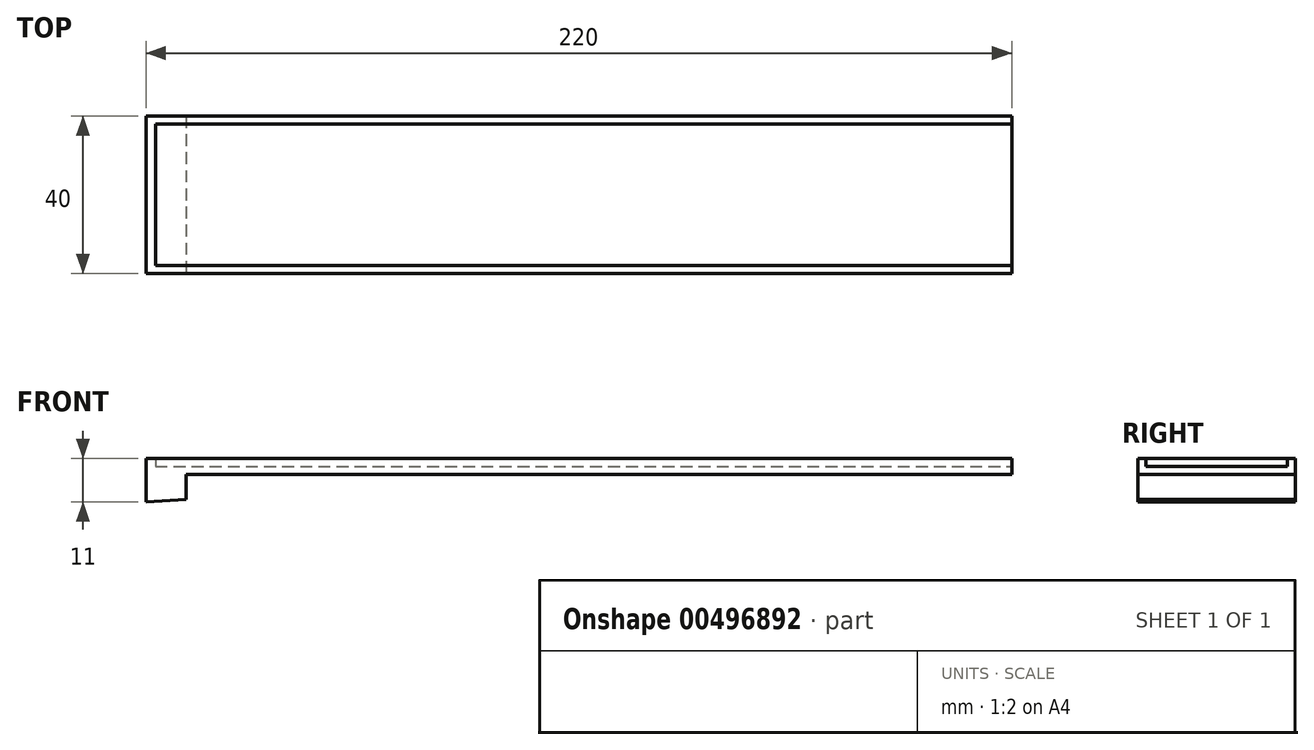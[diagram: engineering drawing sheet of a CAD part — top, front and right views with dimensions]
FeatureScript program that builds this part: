
annotation { "Feature Type Name" : "Feature", "Feature Type Description" : "" }
export const myFeature = defineFeature(function(context is Context, id is Id, definition is map)
    precondition{}
    {
        {
            var Q0;
            Q0=qCreatedBy(makeId("Top.planeOp"),FACE);
            var sketch = newSketch(context, id + "F0", { "sketchPlane" : qUnion([Q0])});
            skLineSegment(sketch, "E0.bottom", {"start": v(-60.42, 25.47) * mm, "end": v(159.58, 25.47) * mm});
            skLineSegment(sketch, "E0.top", {"start": v(-60.42, -14.53) * mm, "end": v(159.58, -14.53) * mm});
            skLineSegment(sketch, "E0.left", {"start": v(-60.42, 25.47) * mm, "end": v(-60.42, -14.53) * mm});
            skLineSegment(sketch, "E0.right", {"start": v(159.58, 25.47) * mm, "end": v(159.58, -14.53) * mm});
            skSolve(sketch);
        }
        {
            var Q0;
            Q0=makeQuery(id+"F0.imprint","IMPRINT",FACE,{"disambiguationData":[TD([[makeQuery(id+"F0.imprint","IMPRINT",EDGE,{"derivedFrom":sQuery(id+"F0.wireOp",EDGE,"E0.bottom")}),-1.0]])]});
            extrude(context, id + "F1", {"entities" : qUnion([Q0]), "depth" : 2 * mm});
        }
        {
            var Q0;
            Q0=makeQuery(id+"F1.opExtrude","CAP_FACE",FACE,{"disambiguationData":[OSD([sQuery(id+"F0.wireOp",EDGE,"E0.bottom"),sQuery(id+"F0.wireOp",EDGE,"E0.top"),sQuery(id+"F0.wireOp",EDGE,"E0.left"),sQuery(id+"F0.wireOp",EDGE,"E0.right")])],"isStart":true});
            var sketch = newSketch(context, id + "F2", { "sketchPlane" : qUnion([Q0])});
            skLineSegment(sketch, "E1.bottom", {"start": v(-60.42, -25.47) * mm, "end": v(-50.23, -25.47) * mm});
            skLineSegment(sketch, "E1.top", {"start": v(-60.42, 14.53) * mm, "end": v(-50.23, 14.53) * mm});
            skLineSegment(sketch, "E1.left", {"start": v(-60.42, -25.47) * mm, "end": v(-60.42, 14.53) * mm});
            skLineSegment(sketch, "E1.right", {"start": v(-50.23, -25.47) * mm, "end": v(-50.23, 14.53) * mm});
            skSolve(sketch);
        }
        {
            var Q0;
            Q0=makeQuery(id+"F2.imprint","IMPRINT",FACE,{"disambiguationData":[TD([[makeQuery(id+"F2.imprint","IMPRINT",EDGE,{"derivedFrom":sQuery(id+"F2.wireOp",EDGE,"E1.bottom")}),1.0]])]});
            extrude(context, id + "F3", {"entities" : qUnion([Q0]), "operationType" : NewBodyOperationType.ADD, "depth" : 7 * mm});
        }
        {
            var Q0;
            Q0=makeQuery(id+"F1.opExtrude","CAP_FACE",FACE,{"disambiguationData":[OSD([sQuery(id+"F0.wireOp",EDGE,"E0.bottom"),sQuery(id+"F0.wireOp",EDGE,"E0.top"),sQuery(id+"F0.wireOp",EDGE,"E0.left"),sQuery(id+"F0.wireOp",EDGE,"E0.right")])],"isStart":false});
            var sketch = newSketch(context, id + "F4", { "sketchPlane" : qUnion([Q0])});
            skLineSegment(sketch, "E2", {"start": v(-60.42, 25.47) * mm, "end": v(-60.42, -14.53) * mm});
            skLineSegment(sketch, "E3", {"start": v(-60.42, -14.53) * mm, "end": v(159.58, -14.53) * mm});
            skLineSegment(sketch, "E4", {"start": v(159.58, -14.53) * mm, "end": v(159.58, -12.53) * mm});
            skLineSegment(sketch, "E5", {"start": v(159.58, -12.53) * mm, "end": v(-57.98, -12.53) * mm});
            skLineSegment(sketch, "E6", {"start": v(-57.98, -12.53) * mm, "end": v(-57.98, 23.47) * mm});
            skLineSegment(sketch, "E7", {"start": v(-57.98, 23.47) * mm, "end": v(159.58, 23.47) * mm});
            skLineSegment(sketch, "E8", {"start": v(159.58, 23.47) * mm, "end": v(159.58, 25.47) * mm});
            skLineSegment(sketch, "E9", {"start": v(159.58, 25.47) * mm, "end": v(-60.42, 25.47) * mm});
            skLineSegment(sketch, "E10", {"start": v(-57.98, 23.47) * mm, "end": v(-57.98, 25.47) * mm, "construction": true});
            skLineSegment(sketch, "E11", {"start": v(-57.98, -12.53) * mm, "end": v(-57.98, -14.53) * mm, "construction": true});
            skSolve(sketch);
        }
        {
            var Q0;
            Q0=makeQuery(id+"F4.imprint","IMPRINT",FACE,{"disambiguationData":[TD([[makeQuery(id+"F4.imprint","IMPRINT",EDGE,{"derivedFrom":sQuery(id+"F4.wireOp",EDGE,"E2")}),1.0]])]});
            extrude(context, id + "F5", {"entities" : qUnion([Q0]), "operationType" : NewBodyOperationType.ADD, "depth" : 2 * mm});
        }
        {
            var Q0;
            Q0=makeQuery(id+"F5.boolean.opBoolean","MERGE",FACE,{"derivedFrom":[makeQuery(id+"F3.boolean.opBoolean","MERGE",FACE,{"derivedFrom":[makeQuery(id+"F1.opExtrude","SWEPT_FACE",FACE,{"disambiguationData":[OSD([sQuery(id+"F0.wireOp",EDGE,"E0.bottom")])]}),makeQuery(id+"F3.opExtrude","SWEPT_FACE",FACE,{"disambiguationData":[OSD([sQuery(id+"F2.wireOp",EDGE,"E1.bottom")])]})]}),makeQuery(id+"F5.opExtrude","SWEPT_FACE",FACE,{"disambiguationData":[OSD([sQuery(id+"F4.wireOp",EDGE,"E9")])]})]});
            var sketch = newSketch(context, id + "F6", { "sketchPlane" : qUnion([Q0])});
            skLineSegment(sketch, "E12", {"start": v(50.23, -7) * mm, "end": v(50.23, -6.4) * mm});
            skLineSegment(sketch, "E13", {"start": v(50.23, -6.4) * mm, "end": v(60.42, -7) * mm});
            skLineSegment(sketch, "E14", {"start": v(60.42, -7) * mm, "end": v(50.23, -7) * mm});
            skSolve(sketch);
        }
        {
            var Q0;
            Q0=makeQuery(id+"F6.imprint","IMPRINT",FACE,{"disambiguationData":[TD([[makeQuery(id+"F6.imprint","IMPRINT",EDGE,{"derivedFrom":sQuery(id+"F6.wireOp",EDGE,"E12")}),-1.0]])]});
            extrude(context, id + "F7", {"entities" : qUnion([Q0]), "operationType" : NewBodyOperationType.REMOVE, "endBound" : BoundingType.THROUGH_ALL, "oppositeDirection" : true, "depth" : 25 * mm});
        }
    });
